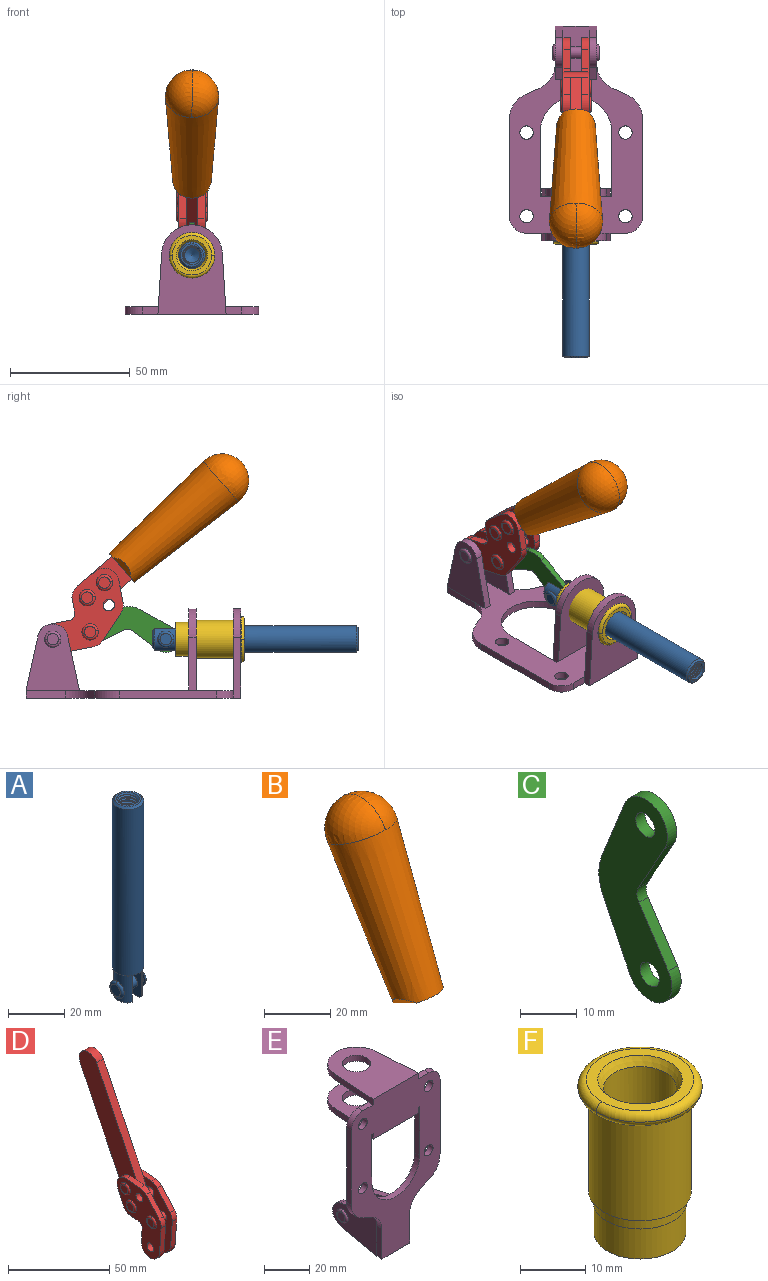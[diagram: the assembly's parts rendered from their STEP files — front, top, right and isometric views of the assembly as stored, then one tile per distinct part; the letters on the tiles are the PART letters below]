
ASSEMBLY  parts=6 mates=6
PART A: 48 faces, bbox 12.6x11.1x86.1 mm
  f0: torus R=2.41mm, axis (-1,0,0), area 15mm2, adj f30,f32,f34
  f1: torus R=2.41mm, axis (-1,0,0), area 15mm2, adj f29,f31,f33
  f2: cylinder r=5.54mm len=72.39mm, axis (0,0,1), area 2518.5mm2, adj f3,f4,f42,f43
  f3: cone r=5.54mm half-angle=45deg, axis (0,0,1), area 7.6mm2, adj f2,f5,f41
  f4: cone r=5.54mm half-angle=45deg, axis (0,0,-1), area 34.9mm2, adj f2,f39
  f5: cylinder r=5.08mm len=11.48mm, axis (0,0,1), area 108.3mm2, adj f3,f7,f8,f41
  f6: cylinder r=2.41mm len=4.83mm, axis (-1,0,0), area 71.2mm2, adj f40,f41
  f7: cylinder r=2.41mm len=4.83mm, axis (-1,0,0), area 7.6mm2, adj f5,f34
  f8: cone r=5.08mm half-angle=45deg, axis (0,0,1), area 10.6mm2, adj f5,f37,f41
  f9: cone r=3.98mm half-angle=45deg, axis (0,0,1), area 17.6mm2, adj f27,f39,f45,f46,f47
  f10: cylinder r=2.41mm len=4.83mm, axis (-1,0,0), area 7.6mm2, adj f33,f38
  f11: cylinder r=3.2mm len=6.4mm, axis (0,0,1), area 78.4mm2, adj f12,f28,f44,f45,f47
  f12: cylinder r=3.2mm len=6.4mm, axis (0,0,1), area 10.5mm2, adj f11,f13,f45,f47
  f13: cylinder r=3.2mm len=6.4mm, axis (0,0,1), area 10.5mm2, adj f12,f14,f45,f47
  f14: cylinder r=3.2mm len=6.4mm, axis (0,0,1), area 10.5mm2, adj f13,f15,f45,f47
  f15: cylinder r=3.2mm len=6.4mm, axis (0,0,1), area 10.5mm2, adj f14,f16,f45,f47
  f16: cylinder r=3.2mm len=6.4mm, axis (0,0,1), area 10.5mm2, adj f15,f17,f45,f47
  f17: cylinder r=3.2mm len=6.4mm, axis (0,0,1), area 10.5mm2, adj f16,f18,f45,f47
  f18: cylinder r=3.2mm len=6.4mm, axis (0,0,1), area 10.5mm2, adj f17,f19,f45,f47
  f19: cylinder r=3.2mm len=6.4mm, axis (0,0,1), area 10.5mm2, adj f18,f20,f45,f47
  f20: cylinder r=3.2mm len=6.4mm, axis (0,0,1), area 10.5mm2, adj f19,f21,f45,f47
  f21: cylinder r=3.2mm len=6.4mm, axis (0,0,1), area 10.5mm2, adj f20,f22,f45,f47
  f22: cylinder r=3.2mm len=6.4mm, axis (0,0,1), area 10.5mm2, adj f21,f23,f45,f47
  f23: cylinder r=3.2mm len=6.4mm, axis (0,0,1), area 10.5mm2, adj f22,f24,f45,f47
  f24: cylinder r=3.2mm len=6.4mm, axis (0,0,1), area 10.5mm2, adj f23,f25,f45,f47
  f25: cylinder r=3.2mm len=6.4mm, axis (0,0,1), area 10.5mm2, adj f24,f26,f45,f47
  f26: cylinder r=3.2mm len=6.4mm, axis (0,0,1), area 10.5mm2, adj f25,f27,f45,f47
  f27: cylinder r=3.2mm len=6.4mm, axis (0,0,1), area 7.4mm2, adj f9,f26,f45,f47
  f28: cone r=3.2mm half-angle=60deg, axis (0,0,1), area 37.2mm2, adj f11
  f29: plane 4.83x4.83mm, normal (-1,0,0), area 18.3mm2, adj f1,f31
  f30: plane 4.83x4.83mm, normal (1,0,0), area 18.3mm2, adj f0,f32
  f31: torus R=2.41mm, axis (-1,0,0), area 15mm2, adj f1,f29,f33
  f32: torus R=2.41mm, axis (-1,0,0), area 15mm2, adj f0,f30,f34
  f33: plane 6.83x6.83mm, normal (1,0,0), area 18.3mm2, adj f1,f10,f31
  f34: plane 6.83x6.83mm, normal (-1,0,0), area 18.3mm2, adj f0,f7,f32
  f35: cone r=5.08mm half-angle=45deg, axis (0,0,1), area 10.6mm2, adj f36,f38,f40
  f36: plane 7.25x1.97mm, normal (0,0,-1), area 10mm2, adj f35,f40
  f37: plane 7.25x1.97mm, normal (0,0,-1), area 10mm2, adj f8,f41
  f38: cylinder r=5.08mm len=11.48mm, axis (0,0,1), area 108.3mm2, adj f10,f35,f40,f42
  f39: plane 9.55x9.55mm, normal (0,0,1), area 22mm2, adj f4,f9
  f40: plane 12.76x10.09mm, normal (1,0,0), area 95.7mm2, adj f6,f35,f36,f38,f42,f43
  f41: plane 12.76x10.09mm, normal (-1,0,0), area 95.7mm2, adj f3,f5,f6,f8,f37,f43
  f42: cone r=5.54mm half-angle=45deg, axis (0,0,1), area 7.6mm2, adj f2,f38,f40
  f43: plane 11.07x4.7mm, normal (0,0,-1), area 50.4mm2, adj f2,f40,f41
  f44: plane 0.89x0.62mm, normal (-1,0,0), area 0.3mm2, adj f11,f45,f46,f47
  f45: bspline ~24.8x7.63mm, area 266.6mm2, adj f9,f11,f12,f13,f14,f15,f16,f17
  f46: bspline ~24.87x7.63mm, area 73.6mm2, adj f9,f44,f45,f47
  f47: bspline ~24.98x7.63mm, area 272.5mm2, adj f9,f11,f12,f13,f14,f15,f16,f17
PART B: 11 faces, bbox 22.3x42.6x64.5 mm
  f0: sphere r=11.13mm, area 411.4mm2, adj f1,f8
  f1: cone r=11.11mm half-angle=3.3deg, axis (0,0.44,0.9), area 3251.8mm2, adj f0,f7,f8,f9,f10
  f2: cylinder r=6.16mm len=11.7mm, axis (1,0,0), area 89.5mm2, adj f3,f4,f5,f6
  f3: plane 60.23x36.75mm, normal (-1,0,0), area 763.6mm2, adj f2,f4,f6,f10
  f4: plane 51.37x25.05mm, normal (0,0.9,-0.44), area 264.2mm2, adj f2,f3,f5,f10
  f5: plane 60.23x36.75mm, normal (1,0,0), area 763.6mm2, adj f2,f4,f6,f10
  f6: plane 51.37x25.05mm, normal (0,-0.9,0.44), area 264.2mm2, adj f2,f3,f5,f10
  f7: plane 9.95x5.95mm, normal (0.71,-0.31,-0.64), area 25.8mm2, adj f1,f10
  f8: sphere r=11.13mm, area 411.4mm2, adj f0,f1
  f9: plane 9.95x5.95mm, normal (-0.71,-0.31,-0.64), area 25.8mm2, adj f1,f10
  f10: plane 14.27x11.38mm, normal (0,-0.44,-0.9), area 106.7mm2, adj f1,f3,f4,f5,f6,f7,f9
PART C: 12 faces, bbox 2.3x18.2x42.8 mm
  f0: cylinder r=2.4mm len=4.8mm, axis (1,0,0), area 34.9mm2, adj f4,f11
  f1: cylinder r=10.41mm len=8.47mm, axis (1,0,0), area 20.2mm2, adj f4,f9,f10,f11
  f2: cylinder r=3.05mm len=3.16mm, axis (1,0,0), area 7.7mm2, adj f4,f6,f7,f11
  f3: cylinder r=2.4mm len=4.8mm, axis (1,0,0), area 34.9mm2, adj f4,f11
  f4: plane 42.81x18.23mm, normal (-1,0,0), area 414.1mm2, adj f0,f1,f2,f3,f5,f6,f7,f8
  f5: cylinder r=5.54mm len=10.67mm, axis (1,0,0), area 41.8mm2, adj f4,f6,f10,f11
  f6: plane 11.66x6.53mm, normal (0,-0.87,-0.49), area 30.9mm2, adj f2,f4,f5,f11
  f7: plane 11.17x7.33mm, normal (0,-0.84,0.55), area 30.9mm2, adj f2,f4,f8,f11
  f8: cylinder r=5.54mm len=10.51mm, axis (1,0,0), area 41.8mm2, adj f4,f7,f9,f11
  f9: plane 13.67x6.67mm, normal (0,0.9,-0.44), area 35.1mm2, adj f1,f4,f8,f11
  f10: plane 14.1x5.7mm, normal (0,0.93,0.37), area 35.1mm2, adj f1,f4,f5,f11
  f11: plane 42.81x18.23mm, normal (1,0,0), area 414.1mm2, adj f0,f1,f2,f3,f5,f6,f7,f8
PART D: 59 faces, bbox 12.9x60.2x99.6 mm
  f0: torus R=2.39mm, axis (-1,0,0), area 14.9mm2, adj f20,f43,f51
  f1: torus R=2.39mm, axis (-1,0,0), area 14.9mm2, adj f19,f42,f51
  f2: torus R=2.39mm, axis (-1,0,0), area 14.9mm2, adj f18,f35,f51
  f3: torus R=2.39mm, axis (-1,0,0), area 14.9mm2, adj f14,f17,f23
  f4: torus R=2.39mm, axis (-1,0,0), area 14.9mm2, adj f13,f16,f23
  f5: torus R=2.39mm, axis (-1,0,0), area 14.9mm2, adj f12,f15,f23
  f6: cylinder r=2.39mm len=4.78mm, axis (1,0,0), area 46.5mm2, adj f48,f50,f51
  f7: cylinder r=2.39mm len=4.78mm, axis (1,0,0), area 46.5mm2, adj f50,f51
  f8: cylinder r=6.35mm len=12.68mm, axis (1,0,0), area 61.8mm2, adj f38,f39,f50,f51
  f9: cylinder r=2.39mm len=4.78mm, axis (-1,0,0), area 70.5mm2, adj f46,f50
  f10: cylinder r=2.39mm len=4.78mm, axis (-1,0,0), area 46.5mm2, adj f23,f45,f46
  f11: cylinder r=2.39mm len=4.78mm, axis (-1,0,0), area 46.5mm2, adj f23,f46
  f12: plane 4.78x4.78mm, normal (1,0,0), area 17.9mm2, adj f5,f15
  f13: plane 4.78x4.78mm, normal (1,0,0), area 17.9mm2, adj f4,f16
  f14: plane 4.78x4.78mm, normal (1,0,0), area 17.9mm2, adj f3,f17
  f15: torus R=2.39mm, axis (-1,0,0), area 14.9mm2, adj f5,f12,f23
  f16: torus R=2.39mm, axis (-1,0,0), area 14.9mm2, adj f4,f13,f23
  f17: torus R=2.39mm, axis (-1,0,0), area 14.9mm2, adj f3,f14,f23
  f18: plane 4.78x4.78mm, normal (-1,0,0), area 17.9mm2, adj f2,f35
  f19: plane 4.78x4.78mm, normal (-1,0,0), area 17.9mm2, adj f1,f42
  f20: plane 4.78x4.78mm, normal (-1,0,0), area 17.9mm2, adj f0,f43
  f21: plane 2.26x0.2mm, normal (1,0,0), area 0.2mm2, adj f31,f44
  f22: plane 2.26x0.2mm, normal (-1,0,0), area 0.2mm2, adj f41,f44
  f23: plane 39.37x30.77mm, normal (1,0,0), area 565.5mm2, adj f3,f4,f5,f10,f11,f15,f16,f17
  f24: cylinder r=6.1mm len=4.15mm, axis (-1,0,0), area 14.7mm2, adj f23,f25,f32,f46
  f25: plane 10.25x9.01mm, normal (0,-0.75,0.66), area 42.3mm2, adj f23,f24,f26,f46
  f26: cylinder r=6.35mm len=4.64mm, axis (-1,0,0), area 15.6mm2, adj f23,f25,f27,f46
  f27: plane 15.84x3.1mm, normal (0,-1,-0.07), area 49.2mm2, adj f23,f26,f28,f46
  f28: cylinder r=6.35mm len=12.68mm, axis (-1,0,0), area 61.8mm2, adj f23,f27,f29,f46
  f29: plane 8.11x3.1mm, normal (0,1,0.07), area 25.2mm2, adj f23,f28,f30,f46
  f30: cylinder r=3.05mm len=3.25mm, axis (-1,0,0), area 14.8mm2, adj f23,f29,f31,f46
  f31: plane 5.99x3.1mm, normal (0,0.07,-1), area 18.6mm2, adj f21,f23,f30,f44,f46
  f32: plane 9.5x3.1mm, normal (0,-0.07,1), area 29.5mm2, adj f23,f24,f33,f46,f47
  f33: cylinder r=6.1mm len=8.63mm, axis (-1,0,0), area 39.1mm2, adj f23,f32,f34,f47
  f34: plane 8.65x3.96mm, normal (0,0.91,-0.42), area 29.5mm2, adj f23,f33,f44,f47
  f35: torus R=2.39mm, axis (-1,0,0), area 14.9mm2, adj f2,f18,f51
  f36: plane 10.25x9.01mm, normal (0,-0.75,0.66), area 42.3mm2, adj f37,f49,f50,f51
  f37: cylinder r=6.35mm len=4.64mm, axis (1,0,0), area 15.6mm2, adj f36,f38,f50,f51
  f38: plane 15.84x3.1mm, normal (0,-1,-0.07), area 49.2mm2, adj f8,f37,f50,f51
  f39: plane 8.11x3.1mm, normal (0,1,0.07), area 25.2mm2, adj f8,f40,f50,f51
  f40: cylinder r=3.05mm len=3.25mm, axis (1,0,0), area 14.8mm2, adj f39,f41,f50,f51
  f41: plane 5.99x3.1mm, normal (0,0.07,-1), area 18.6mm2, adj f22,f40,f44,f50,f51
  f42: torus R=2.39mm, axis (-1,0,0), area 14.9mm2, adj f1,f19,f51
  f43: torus R=2.39mm, axis (-1,0,0), area 14.9mm2, adj f0,f20,f51
  f44: cylinder r=6.35mm len=12.12mm, axis (-1,0,0), area 128.9mm2, adj f21,f22,f23,f31,f34,f41,f46,f47
  f45: plane 2.65x1.35mm, normal (1,0,0), area 1mm2, adj f10,f55
  f46: plane 39.08x20.42mm, normal (-1,0,0), area 412.5mm2, adj f9,f10,f11,f24,f25,f26,f27,f28
  f47: plane 77.62x39.82mm, normal (1,0,0), area 850mm2, adj f32,f33,f34,f44,f53,f54,f55
  f48: plane 2.65x1.35mm, normal (-1,0,0), area 1mm2, adj f6,f55
  f49: cylinder r=6.1mm len=4.15mm, axis (1,0,0), area 14.7mm2, adj f36,f50,f51,f56
  f50: plane 39.08x20.42mm, normal (1,0,0), area 412.5mm2, adj f6,f7,f8,f9,f36,f37,f38,f39
  f51: plane 39.37x30.77mm, normal (-1,0,0), area 565.5mm2, adj f0,f1,f2,f6,f7,f8,f35,f36
  f52: plane 8.65x3.96mm, normal (0,0.91,-0.42), area 29.5mm2, adj f44,f51,f57,f58
  f53: plane 68.49x33.4mm, normal (0,0.9,-0.44), area 358.1mm2, adj f44,f47,f54,f58
  f54: cylinder r=6.35mm len=12.06mm, axis (1,0,0), area 93.7mm2, adj f47,f53,f55,f58
  f55: plane 68.49x33.4mm, normal (0,-0.9,0.44), area 358.1mm2, adj f44,f45,f46,f47,f48,f50,f54,f58
  f56: plane 9.5x3.1mm, normal (0,-0.07,1), area 29.5mm2, adj f49,f50,f51,f57,f58
  f57: cylinder r=6.1mm len=8.63mm, axis (1,0,0), area 39.1mm2, adj f51,f52,f56,f58
  f58: plane 77.62x39.82mm, normal (-1,0,0), area 850mm2, adj f44,f52,f53,f54,f55,f56,f57
PART E: 55 faces, bbox 55.7x37.4x89.8 mm
  f0: torus R=2.41mm, axis (-1,0,0), area 15mm2, adj f11,f15,f25
  f1: torus R=2.41mm, axis (-1,0,0), area 15mm2, adj f10,f12,f22
  f2: cylinder r=2.78mm len=5.56mm, axis (0,-1,0), area 54.2mm2, adj f30,f54
  f3: cylinder r=14.99mm len=29.97mm, axis (0,-1,0), area 145.9mm2, adj f30,f49,f53,f54
  f4: cylinder r=2.78mm len=5.56mm, axis (0,-1,0), area 54.2mm2, adj f30,f54
  f5: cylinder r=2.78mm len=5.56mm, axis (0,-1,0), area 54.2mm2, adj f30,f54
  f6: cylinder r=2.78mm len=5.56mm, axis (0,-1,0), area 54.2mm2, adj f30,f54
  f7: cylinder r=6.35mm len=12.7mm, axis (0,0,1), area 123.6mm2, adj f27,f51
  f8: cylinder r=6.35mm len=12.7mm, axis (0,0,-1), area 124.7mm2, adj f21,f35
  f9: cylinder r=2.41mm len=11.18mm, axis (-1,0,0), area 169.4mm2, adj f16,f19
  f10: plane 4.83x4.83mm, normal (1,0,0), area 18.3mm2, adj f1,f12
  f11: plane 4.83x4.83mm, normal (-1,0,0), area 18.3mm2, adj f0,f15
  f12: torus R=2.41mm, axis (-1,0,0), area 15mm2, adj f1,f10,f22
  f13: cylinder r=6.35mm len=12.41mm, axis (1,0,0), area 53.4mm2, adj f18,f19,f22,f23
  f14: cylinder r=6.35mm len=12.41mm, axis (-1,0,0), area 53.4mm2, adj f16,f17,f24,f25
  f15: torus R=2.41mm, axis (-1,0,0), area 15mm2, adj f0,f11,f25
  f16: plane 27.86x22.35mm, normal (1,0,0), area 425.4mm2, adj f9,f14,f17,f24,f30
  f17: plane 22.86x4.97mm, normal (0,0.21,0.98), area 72.5mm2, adj f14,f16,f25,f30
  f18: plane 22.86x4.97mm, normal (0,0.21,0.98), area 72.5mm2, adj f13,f19,f22,f30
  f19: plane 27.86x22.35mm, normal (-1,0,0), area 425.4mm2, adj f9,f13,f18,f23,f30
  f20: cylinder r=12.7mm len=25.35mm, axis (0,0,-1), area 119.8mm2, adj f21,f34,f35,f36
  f21: plane 34.21x28.07mm, normal (0,0,-1), area 702.4mm2, adj f8,f20,f30,f34,f36
  f22: plane 27.96x22.45mm, normal (1,0,0), area 407.2mm2, adj f1,f12,f13,f18,f23,f30,f42,f43
  f23: plane 22.86x4.97mm, normal (0,0.21,-0.98), area 72.5mm2, adj f13,f19,f22,f44
  f24: plane 22.86x4.97mm, normal (0,0.21,-0.98), area 72.5mm2, adj f14,f16,f25,f44
  f25: plane 27.86x22.35mm, normal (-1,0,0), area 407.1mm2, adj f0,f14,f15,f17,f24,f30,f45,f46
  f26: plane 3.1x0.95mm, normal (0,0,-1), area 2.7mm2, adj f30,f49,f50,f54
  f27: plane 34.21x28.07mm, normal (0,0,1), area 702.4mm2, adj f7,f28,f30,f50,f52
  f28: cylinder r=12.7mm len=25.35mm, axis (0,0,1), area 118.8mm2, adj f27,f50,f51,f52
  f29: plane 3.1x0.95mm, normal (0,0,-1), area 2.7mm2, adj f30,f52,f53,f54
  f30: plane 86.54x55.63mm, normal (0,1,0), area 2362.9mm2, adj f2,f3,f4,f5,f6,f16,f17,f18
  f31: plane 40.56x3.1mm, normal (-1,0,0), area 125.7mm2, adj f30,f32,f48,f54
  f32: cylinder r=7.11mm len=7.11mm, axis (0,-1,0), area 34.6mm2, adj f30,f31,f33,f54
  f33: plane 6.67x3.1mm, normal (0,0,1), area 20.4mm2, adj f30,f32,f34,f54
  f34: plane 25.39x3.13mm, normal (-1,0.06,0), area 79.5mm2, adj f20,f21,f33,f35,f54
  f35: plane 37.31x28.45mm, normal (0,0,1), area 789.9mm2, adj f8,f20,f34,f36,f54
  f36: plane 25.39x3.13mm, normal (1,0.06,0), area 79.5mm2, adj f20,f21,f35,f37,f54
  f37: plane 6.67x3.1mm, normal (0,0,1), area 20.4mm2, adj f30,f36,f38,f54
  f38: cylinder r=7.11mm len=7.11mm, axis (0,-1,0), area 34.6mm2, adj f30,f37,f39,f54
  f39: plane 40.56x3.1mm, normal (1,0,0), area 125.7mm2, adj f30,f38,f40,f54
  f40: cylinder r=11.18mm len=10.16mm, axis (0,-1,0), area 39.5mm2, adj f30,f39,f41,f54
  f41: plane 6.09x3.1mm, normal (0.42,0,-0.91), area 20.8mm2, adj f30,f40,f42,f54
  f42: cylinder r=11.18mm len=9.41mm, axis (0,-1,0), area 37.2mm2, adj f22,f30,f41,f43,f54
  f43: plane 16.5x3.1mm, normal (1,0,0), area 51.1mm2, adj f22,f42,f44,f54
  f44: plane 17.37x3.1mm, normal (0,0,-1), area 53.8mm2, adj f23,f24,f30,f43,f45,f54
  f45: plane 16.5x3.1mm, normal (-1,0,0), area 51.1mm2, adj f25,f44,f46,f54
  f46: cylinder r=11.18mm len=9.41mm, axis (0,-1,0), area 37.2mm2, adj f25,f30,f45,f47,f54
  f47: plane 6.09x3.1mm, normal (-0.42,0,-0.91), area 20.8mm2, adj f30,f46,f48,f54
  f48: cylinder r=11.18mm len=10.16mm, axis (0,-1,0), area 39.5mm2, adj f30,f31,f47,f54
  f49: plane 26.54x3.1mm, normal (-1,0,0), area 82.3mm2, adj f3,f26,f30,f54
  f50: plane 25.39x3.1mm, normal (1,0.06,0), area 78.8mm2, adj f26,f27,f28,f51,f54
  f51: plane 37.31x28.45mm, normal (0,0,-1), area 789.9mm2, adj f7,f28,f50,f52,f54
  f52: plane 25.39x3.1mm, normal (-1,0.06,0), area 78.8mm2, adj f27,f28,f29,f51,f54
  f53: plane 26.54x3.1mm, normal (1,0,0), area 82.3mm2, adj f3,f29,f30,f54
  f54: plane 89.66x55.63mm, normal (0,-1,0), area 2678.5mm2, adj f2,f3,f4,f5,f6,f26,f29,f31
PART F: 15 faces, bbox 20.6x20.6x28.7 mm
  f0: torus R=8.26mm, axis (0,0,1), area 56.8mm2, adj f1,f10,f12
  f1: torus R=8.26mm, axis (0,0,1), area 56.8mm2, adj f0,f6,f13
  f2: cylinder r=5.59mm len=25.91mm, axis (0,0,1), area 909.6mm2, adj f3,f4
  f3: cone r=6.86mm half-angle=45deg, axis (0,0,-1), area 70.2mm2, adj f2,f14
  f4: cone r=6.47mm half-angle=30deg, axis (0,0,1), area 66.7mm2, adj f2,f13
  f5: cylinder r=7.04mm len=14.07mm, axis (0,0,1), area 252.6mm2, adj f11,f14
  f6: torus R=8.26mm, axis (0,0,1), area 56.8mm2, adj f1,f12,f13
  f7: cylinder r=7.16mm len=14.33mm, axis (0,0,1), area 91.5mm2, adj f9,f11
  f8: cylinder r=7.86mm len=18.42mm, axis (0,0,1), area 909.6mm2, adj f9,f10
  f9: plane 15.72x15.72mm, normal (0,0,-1), area 33mm2, adj f7,f8
  f10: plane 16.51x16.51mm, normal (0,0,-1), area 19.9mm2, adj f0,f8,f12
  f11: plane 14.33x14.33mm, normal (0,0,-1), area 5.7mm2, adj f5,f7
  f12: torus R=8.26mm, axis (0,0,1), area 56.8mm2, adj f0,f6,f10
  f13: plane 16.51x16.51mm, normal (0,0,1), area 82.7mm2, adj f1,f4,f6
  f14: plane 14.07x14.07mm, normal (0,0,-1), area 7.8mm2, adj f3,f5
PLACE A rot(axis=(1,0,0),90deg) t=(0,1.94,-18.66)mm
PLACE B rot(axis=(1,0,0),75deg) t=(0,-3.72,-9.51)mm
PLACE C rot(axis=(1,0,0),97.5deg) t=(0,5.01,-16.43)mm
PLACE D rot(axis=(1,0,0),75deg) t=(0,-3.72,-9.51)mm
PLACE E rot(axis=(1,0,0),90deg) t=(0,1.56,-18.66)mm fixed
PLACE F rot(axis=(1,0,0),90deg) t=(0,2.58,-18.66)mm
MATE fastened B.f2 <-> D.f54  axis (1,0,0) through (0,-38.24,73.28)mm
MATE revolute C.f5 <-> A.f6  axis (1,0,0) through (0,-13.53,5.96)mm
MATE revolute C.f3 <-> D.f4  axis (1,0,0) through (0,18.07,8.99)mm
MATE fastened F.f2 <-> E.f7  axis (0,-1,0) through (0,-44.83,5.96)mm
MATE revolute D.f7 <-> E.f0  axis (-1,0,0) through (0,33.65,5.96)mm
MATE slider A.f2 <-> F.f2  axis (0,-1,0) through (0,-56.84,5.96)mm
